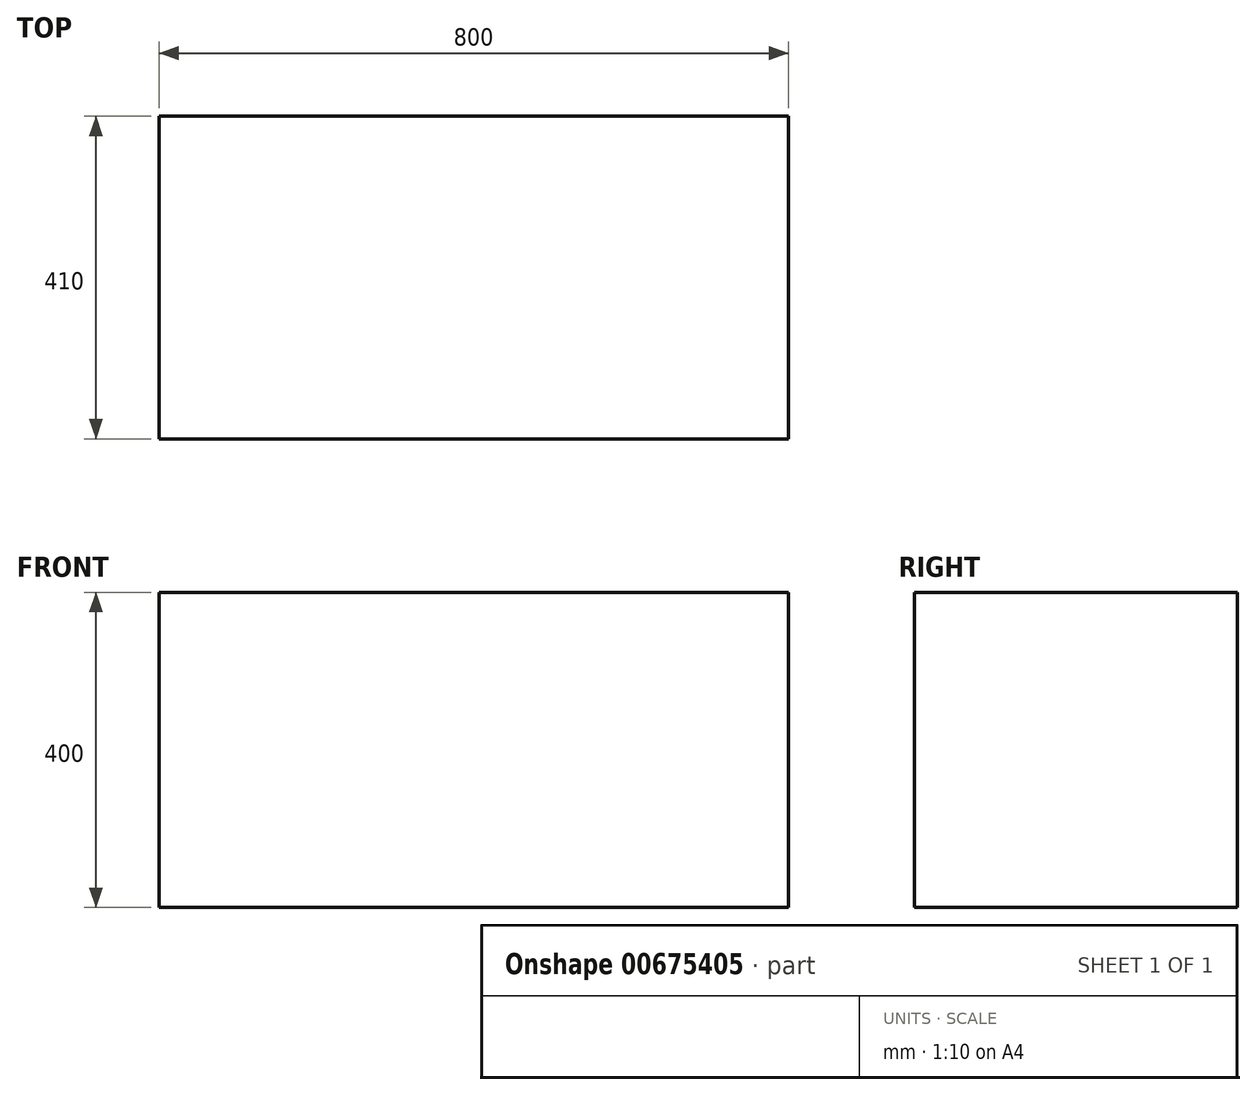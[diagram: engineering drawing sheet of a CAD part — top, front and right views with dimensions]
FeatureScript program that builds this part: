
annotation { "Feature Type Name" : "Feature", "Feature Type Description" : "" }
export const myFeature = defineFeature(function(context is Context, id is Id, definition is map)
    precondition{}
    {
        {
            var Q0;
            Q0=qCreatedBy(makeId("Top.planeOp"),FACE);
            var sketch = newSketch(context, id + "F0", { "sketchPlane" : qUnion([Q0])});
            skLineSegment(sketch, "E0.bottom", {"start": v(400, 205) * mm, "end": v(-400, 205) * mm});
            skLineSegment(sketch, "E0.top", {"start": v(400, -205) * mm, "end": v(-400, -205) * mm});
            skLineSegment(sketch, "E0.left", {"start": v(400, 205) * mm, "end": v(400, -205) * mm});
            skLineSegment(sketch, "E0.right", {"start": v(-400, 205) * mm, "end": v(-400, -205) * mm});
            skPoint(sketch, "E0.middle", {"position": v(0, 0) * mm});
            skSolve(sketch);
        }
        {
            var Q0;
            Q0 = qSketchRegion(id + "F0", true);
            extrude(context, id + "F1", {"entities" : qUnion([Q0]), "depth" : 400 * mm, "offsetDistance" : 25.4 * mm});
        }
    });
